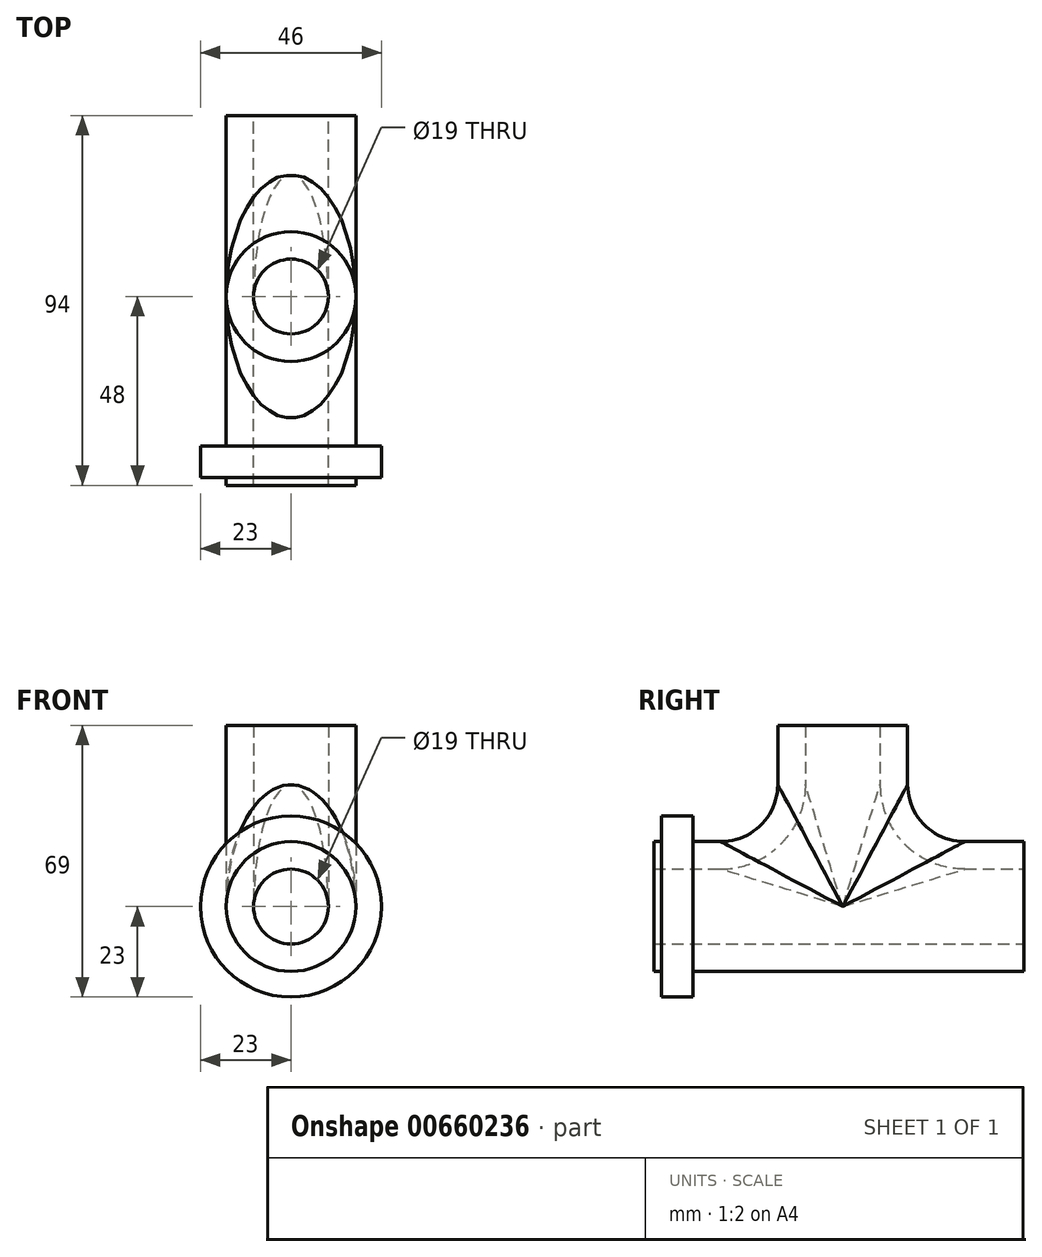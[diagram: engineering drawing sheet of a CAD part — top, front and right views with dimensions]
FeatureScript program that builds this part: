
annotation { "Feature Type Name" : "Feature", "Feature Type Description" : "" }
export const myFeature = defineFeature(function(context is Context, id is Id, definition is map)
    precondition{}
    {
        {
            var Q0;
            Q0=qCreatedBy(makeId("Front.planeOp"),FACE);
            var sketch = newSketch(context, id + "F0", { "sketchPlane" : qUnion([Q0])});
            skCircle(sketch, "E0", {"center": v(0, 0) * mm, "radius": 16.5 * mm});
            skSolve(sketch);
        }
        {
            var Q0;
            Q0=qCreatedBy(makeId("Top.planeOp"),FACE);
            var sketch = newSketch(context, id + "F1", { "sketchPlane" : qUnion([Q0])});
            skCircle(sketch, "E1", {"center": v(0, 0) * mm, "radius": 16.5 * mm});
            skSolve(sketch);
        }
        {
            var Q0;
            Q0 = qSketchRegion(id + "F0", true);
            extrude(context, id + "F2", {"entities" : qUnion([Q0]), "depth" : 46 * mm, "offsetDistance" : 25 * mm, "hasSecondDirection" : true, "secondDirectionOppositeDirection" : true, "secondDirectionDepth" : 46 * mm});
        }
        {
            var Q0;
            Q0 = qSketchRegion(id + "F1", true);
            extrude(context, id + "F3", {"entities" : qUnion([Q0]), "operationType" : NewBodyOperationType.ADD, "depth" : 46 * mm, "offsetDistance" : 25 * mm});
        }
        {
            var Q0;
            Q0=makeQuery(id+"F3.boolean.opBoolean","INTERSECT",EDGE,{"disambiguationData":[OD(0.0)],"derivedFrom":[makeQuery(id+"F2.opExtrude","SWEPT_FACE",FACE,{"disambiguationData":[OSD([sQuery(id+"F0.wireOp",EDGE,"E0")])]}),makeQuery(id+"F3.opExtrude","SWEPT_FACE",FACE,{"disambiguationData":[OSD([sQuery(id+"F1.wireOp",EDGE,"E1")])]})]});
            var Q1;
            Q1=makeQuery(id+"F3.boolean.opBoolean","INTERSECT",EDGE,{"disambiguationData":[OD(1.0)],"derivedFrom":[makeQuery(id+"F2.opExtrude","SWEPT_FACE",FACE,{"disambiguationData":[OSD([sQuery(id+"F0.wireOp",EDGE,"E0")])]}),makeQuery(id+"F3.opExtrude","SWEPT_FACE",FACE,{"disambiguationData":[OSD([sQuery(id+"F1.wireOp",EDGE,"E1")])]})]});
            fillet(context, id + "F4", {"entities" : qUnion([Q0, Q1]), "radius" : 14.5 * mm, "tangentPropagation" : true, "allowEdgeOverflow" : false});
        }
        {
            var Q0;
            Q0=makeQuery(id+"F3.opExtrude","CAP_FACE",FACE,{"disambiguationData":[OSD([sQuery(id+"F1.wireOp",EDGE,"E1")])],"isStart":false});
            var Q1;
            Q1=makeQuery(id+"F2.opExtrude","CAP_FACE",FACE,{"disambiguationData":[OSD([sQuery(id+"F0.wireOp",EDGE,"E0")])],"isStart":false});
            var Q2;
            Q2=makeQuery(id+"F2.opExtrude","CAP_FACE",FACE,{"disambiguationData":[OSD([sQuery(id+"F0.wireOp",EDGE,"E0")])],"isStart":true});
            shell(context, id + "F5", {"entities" : qUnion([Q0, Q1, Q2]), "thickness" : 7 * mm});
        }
        {
            var Q0;
            Q0=makeQuery(id+"F2.opExtrude","CAP_FACE",FACE,{"disambiguationData":[OSD([sQuery(id+"F0.wireOp",EDGE,"E0")])],"isStart":false});
            var sketch = newSketch(context, id + "F6", { "sketchPlane" : qUnion([Q0])});
            skCircle(sketch, "E2", {"center": v(0, 0) * mm, "radius": 23 * mm});
            skSolve(sketch);
        }
        {
            var Q0;
            Q0 = qSketchRegion(id + "F6", true);
            extrude(context, id + "F7", {"entities" : qUnion([Q0]), "operationType" : NewBodyOperationType.ADD, "oppositeDirection" : true, "depth" : 8 * mm, "offsetDistance" : 25 * mm});
        }
        {
            var Q0;
            {var subQ0=sQuery(id+"F0.wireOp",EDGE,"E0");var subQ1=makeQuery(id+"F2.opExtrude","CAP_EDGE",EDGE,{"disambiguationData":[OSD([subQ0])],"isStart":false});Q0=makeQuery(id+"F6.imprint","IMPRINT",FACE,{"disambiguationData":[TD([[makeQuery(id+"F6.imprint","IMPRINT",EDGE,{"derivedFrom":subQ1}),1.0]])]});}
            extrude(context, id + "F8", {"entities" : qUnion([Q0]), "operationType" : NewBodyOperationType.ADD, "depth" : 2 * mm, "offsetDistance" : 25 * mm});
        }
        {
            var Q0;
            {var subQ0=sQuery(id+"F0.wireOp",EDGE,"E0");Q0=makeQuery(id+"F6.imprint","IMPRINT",FACE,{"disambiguationData":[TD([[makeQuery(id+"F6.imprint","IMPRINT",EDGE,{"derivedFrom":makeQuery(id+"F5.opShell","OFFSET_EDGE",EDGE,{"disambiguationData":[OSD([subQ0]),TDD([makeQuery(id+"F2.opExtrude","CAP_EDGE",EDGE,{"disambiguationData":[OSD([subQ0])],"isStart":false})])]})}),1.0]])]});}
            extrude(context, id + "F9", {"entities" : qUnion([Q0]), "operationType" : NewBodyOperationType.REMOVE, "oppositeDirection" : true, "depth" : 188.7 * mm, "offsetDistance" : 25 * mm});
        }
    });
